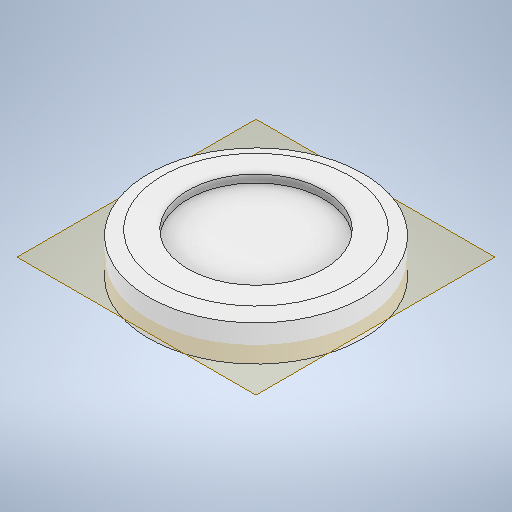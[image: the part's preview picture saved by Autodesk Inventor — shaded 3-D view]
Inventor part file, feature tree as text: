
AUTODESK INVENTOR PART (.ipt)
format: ipt  version: 2025.1 (Build 291241020, 241B)  size: 622,592 bytes
history: native  units: in
note: dims shown in document units (in); Inventor stores cm internally (conversion verified against a paired STEP export)
features: extrude x4, sketch x4, chamfer x2, plane x1, mirror x1
ambient origin geometry x8: Origin, YZ Plane, XZ Plane, XY Plane, X Axis, Y Axis, Z Axis, Center Point
bodies: Solid1 (feature_tree)
feature tree (12):
  extrude  "Extrusion1"  Depth=1.0in
  plane  "Work Plane1"
  extrude  "Extrusion2"  Depth=0.0441in
  extrude  "Extrusion3"  Depth=0.0112in TaperAngle=0.0deg
  extrude  "Extrusion4"  Depth=0.0787in
  chamfer  "Chamfer1"  [1 undecoded]
  chamfer  "Chamfer2"  [1 undecoded]
  sketch  "Sketch1"  dims[d0=1.0in d1=0.0in d2=0.7874in]
  sketch  "Sketch2"  dims[d3=0.0441in d4=0.0in d5=1.2402in]
  sketch  "Sketch3"  dims[d6=0.0in d7=0.0in d8=0.0112in d9=0.0in]
  sketch  "Sketch4"  dims[d10=0.0787in d11=0.0787in d12=0.1374in d13=0.0787in d14=0.0787in d15=0.1374in]
  mirror  "Mirror1"
note: 2 required parameter values undecoded (feature->parameter linkage not recoverable at this tier; creation-order binding heuristic only, values carry confidence <= 0.55)
